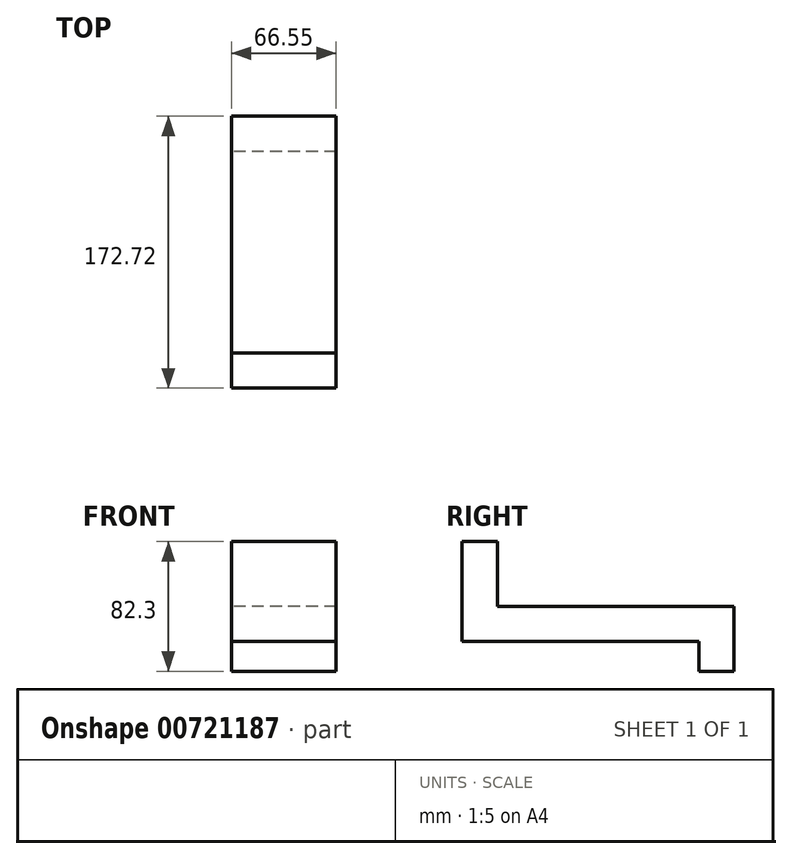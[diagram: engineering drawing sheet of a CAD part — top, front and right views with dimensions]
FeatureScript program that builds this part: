
annotation { "Feature Type Name" : "Feature", "Feature Type Description" : "" }
export const myFeature = defineFeature(function(context is Context, id is Id, definition is map)
    precondition{}
    {
        {
            var Q0;
            Q0=qCreatedBy(makeId("Right.planeOp"),FACE);
            var sketch = newSketch(context, id + "F0", { "sketchPlane" : qUnion([Q0])});
            skLineSegment(sketch, "E0", {"start": v(-71.7, 66.92) * mm, "end": v(-71.7, 3.42) * mm});
            skLineSegment(sketch, "E1", {"start": v(-71.7, 3.42) * mm, "end": v(78.67, 3.42) * mm});
            skLineSegment(sketch, "E2", {"start": v(78.67, 3.42) * mm, "end": v(78.67, -15.38) * mm});
            skLineSegment(sketch, "E3", {"start": v(78.67, -15.38) * mm, "end": v(101.02, -15.38) * mm});
            skLineSegment(sketch, "E4", {"start": v(-71.7, 66.92) * mm, "end": v(-49.34, 66.92) * mm});
            skLineSegment(sketch, "E5", {"start": v(101.02, -15.38) * mm, "end": v(101.02, 25.77) * mm});
            skLineSegment(sketch, "E6", {"start": v(101.02, 25.77) * mm, "end": v(-49.34, 25.77) * mm});
            skLineSegment(sketch, "E7", {"start": v(-49.34, 66.92) * mm, "end": v(-49.34, 25.77) * mm});
            skSolve(sketch);
        }
        {
            var Q0;
            Q0=makeQuery(id+"F0.imprint","IMPRINT",FACE,{"disambiguationData":[TD([[makeQuery(id+"F0.imprint","IMPRINT",EDGE,{"derivedFrom":sQuery(id+"F0.wireOp",EDGE,"E0")}),1.0]])]});
            extrude(context, id + "F1", {"entities" : qUnion([Q0]), "depth" : 66.55 * mm, "offsetDistance" : 25.4 * mm});
        }
    });
